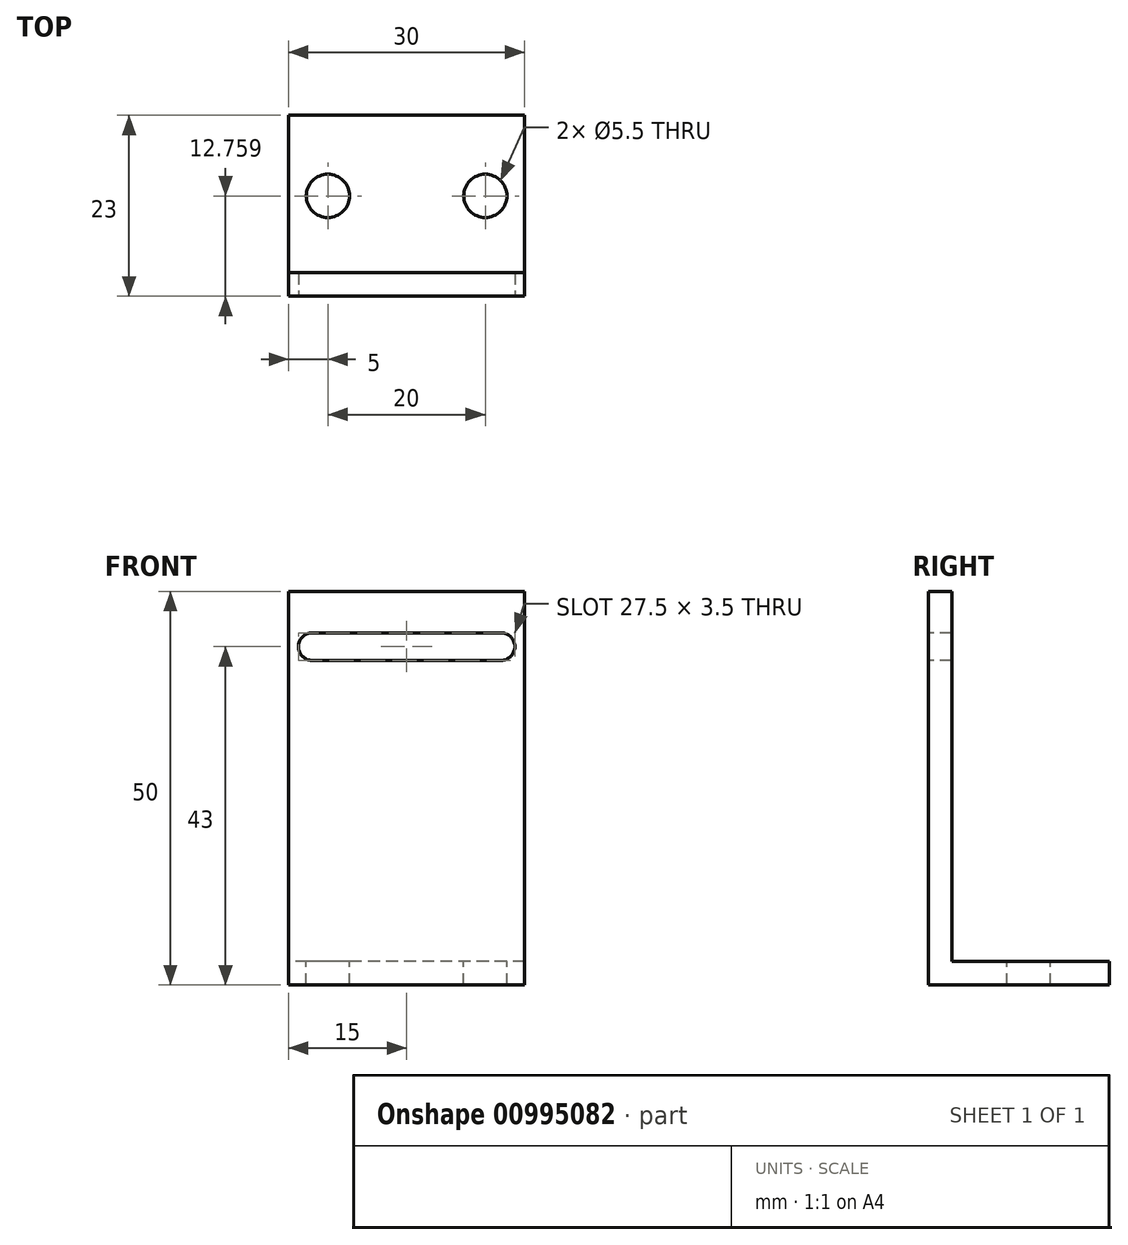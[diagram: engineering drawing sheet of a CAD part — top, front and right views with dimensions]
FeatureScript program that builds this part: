
annotation { "Feature Type Name" : "Feature", "Feature Type Description" : "" }
export const myFeature = defineFeature(function(context is Context, id is Id, definition is map)
    precondition{}
    {
        {
            var Q0;
            Q0=qCreatedBy(makeId("Front.planeOp"),FACE);
            var sketch = newSketch(context, id + "F0", { "sketchPlane" : qUnion([Q0])});
            skLineSegment(sketch, "E0.bottom", {"start": v(-12.5, 50) * mm, "end": v(17.5, 50) * mm});
            skLineSegment(sketch, "E0.top", {"start": v(-12.5, 0) * mm, "end": v(17.5, 0) * mm});
            skLineSegment(sketch, "E0.left", {"start": v(-12.5, 50) * mm, "end": v(-12.5, 0) * mm});
            skLineSegment(sketch, "E0.right", {"start": v(17.5, 50) * mm, "end": v(17.5, 0) * mm});
            skSolve(sketch);
        }
        {
            var Q0;
            Q0 = qSketchRegion(id + "F0", true);
            extrude(context, id + "F1", {"entities" : qUnion([Q0]), "depth" : 3 * mm, "offsetDistance" : 25 * mm});
        }
        {
            var Q0;
            Q0=makeQuery(id+"F1.opExtrude","CAP_FACE",FACE,{"disambiguationData":[OSD([sQuery(id+"F0.wireOp",EDGE,"E0.bottom"),sQuery(id+"F0.wireOp",EDGE,"E0.top"),sQuery(id+"F0.wireOp",EDGE,"E0.left"),sQuery(id+"F0.wireOp",EDGE,"E0.right")])],"isStart":true});
            var sketch = newSketch(context, id + "F2", { "sketchPlane" : qUnion([Q0])});
            skLineSegment(sketch, "E1.bottom", {"start": v(-17.5, 0) * mm, "end": v(12.5, 0) * mm});
            skLineSegment(sketch, "E1.top", {"start": v(-17.5, 3) * mm, "end": v(12.5, 3) * mm});
            skLineSegment(sketch, "E1.left", {"start": v(-17.5, 0) * mm, "end": v(-17.5, 3) * mm});
            skLineSegment(sketch, "E1.right", {"start": v(12.5, 0) * mm, "end": v(12.5, 3) * mm});
            skSolve(sketch);
        }
        {
            var Q0;
            Q0 = qSketchRegion(id + "F2", true);
            extrude(context, id + "F3", {"entities" : qUnion([Q0]), "operationType" : NewBodyOperationType.ADD, "depth" : 20 * mm, "offsetDistance" : 25 * mm});
        }
        {
            var Q0;
            Q0=makeQuery(id+"F3.opExtrude","SWEPT_FACE",FACE,{"disambiguationData":[OSD([sQuery(id+"F2.wireOp",EDGE,"E1.top")])]});
            var sketch = newSketch(context, id + "F4", { "sketchPlane" : qUnion([Q0])});
            skCircle(sketch, "E2", {"center": v(12.5, 9.76) * mm, "radius": 2.75 * mm});
            skCircle(sketch, "E3", {"center": v(-7.5, 9.76) * mm, "radius": 2.75 * mm});
            skSolve(sketch);
        }
        {
            var Q0;
            Q0 = qSketchRegion(id + "F4", true);
            extrude(context, id + "F5", {"entities" : qUnion([Q0]), "operationType" : NewBodyOperationType.REMOVE, "endBound" : BoundingType.THROUGH_ALL, "oppositeDirection" : true, "depth" : 25 * mm, "offsetDistance" : 25 * mm});
        }
        {
            var Q0;
            Q0=makeQuery(id+"F1.opExtrude","CAP_FACE",FACE,{"disambiguationData":[OSD([sQuery(id+"F0.wireOp",EDGE,"E0.bottom"),sQuery(id+"F0.wireOp",EDGE,"E0.top"),sQuery(id+"F0.wireOp",EDGE,"E0.left"),sQuery(id+"F0.wireOp",EDGE,"E0.right")])],"isStart":false});
            var sketch = newSketch(context, id + "F6", { "sketchPlane" : qUnion([Q0])});
            skArc(sketch, "E4", {"start": v(-9.5, 44.75) * mm, "mid": v(-11.25, 43) * mm, "end": v(-9.5, 41.25) * mm});
            skArc(sketch, "E5", {"start": v(14.5, 41.25) * mm, "mid": v(16.25, 43) * mm, "end": v(14.5, 44.75) * mm});
            skLineSegment(sketch, "E6", {"start": v(-9.5, 44.75) * mm, "end": v(14.5, 44.75) * mm});
            skLineSegment(sketch, "E7", {"start": v(-9.5, 41.25) * mm, "end": v(14.5, 41.25) * mm});
            skSolve(sketch);
        }
        {
            var Q0;
            Q0 = qSketchRegion(id + "F6", true);
            extrude(context, id + "F7", {"entities" : qUnion([Q0]), "operationType" : NewBodyOperationType.REMOVE, "endBound" : BoundingType.THROUGH_ALL, "oppositeDirection" : true, "depth" : 25 * mm, "offsetDistance" : 25 * mm});
        }
    });
